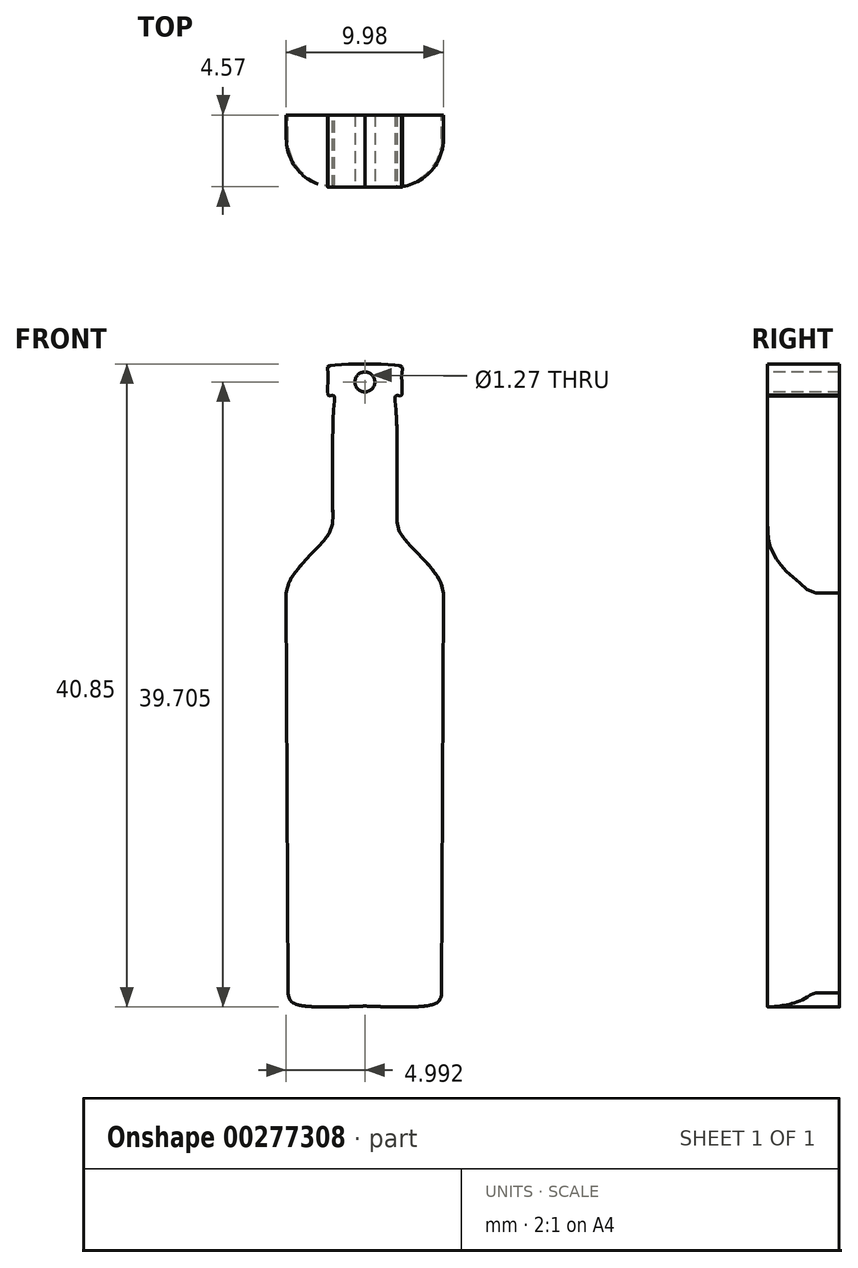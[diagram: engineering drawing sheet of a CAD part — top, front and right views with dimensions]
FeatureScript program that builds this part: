
annotation { "Feature Type Name" : "Feature", "Feature Type Description" : "" }
export const myFeature = defineFeature(function(context is Context, id is Id, definition is map)
    precondition{}
    {
        {
            var Q0;
            Q0=qCreatedBy(makeId("Front.planeOp"),FACE);
            var sketch = newSketch(context, id + "F0", { "sketchPlane" : qUnion([Q0])});
            skLineSegment(sketch, "E0", {"start": v(26.9, -30.26) * mm, "end": v(26.8, -4.86) * mm});
            skFitSpline(sketch, "E1", {"points": [v(26.8, -4.86) * mm, v(27.1, -3.94) * mm, v(28.53, -2.22) * mm, v(29.63, -0.84) * mm, v(29.74, 0.33) * mm, v(29.74, 2.9) * mm, v(29.8, 6.72) * mm, v(29.82, 7.68) * mm, v(29.66, 7.7) * mm, v(29.45, 7.71) * mm, v(29.44, 9.1) * mm, v(29.5, 9.55) * mm, v(31.72, 9.7) * mm, v(31.78, 9.7) * mm], "startDerivative": vector(2.33, 12.28) * mm, "endDerivative": vector(1.3, 0.77) * mm});
            skPoint(sketch, "E2", {"position": v(31.78, -31.09) * mm});
            skFitSpline(sketch, "E3", {"points": [v(26.9, -30.26) * mm, v(27.15, -30.83) * mm, v(28.84, -31.14) * mm, v(31.78, -31.09) * mm], "startDerivative": vector(0.53, -3.07) * mm, "endDerivative": vector(6.67, 0.25) * mm});
            skLineSegment(sketch, "E4", {"start": v(31.78, -31.09) * mm, "end": v(31.78, 9.7) * mm, "construction": true});
            skFitSpline(sketch, "E5.MirrorCS", {"points": [v(36.77, -4.86) * mm, v(36.47, -3.94) * mm, v(35.04, -2.22) * mm, v(33.94, -0.84) * mm, v(33.82, 0.33) * mm, v(33.82, 2.9) * mm, v(33.76, 6.72) * mm, v(33.74, 7.68) * mm, v(33.9, 7.7) * mm, v(34.11, 7.71) * mm, v(34.12, 9.1) * mm, v(34.06, 9.55) * mm, v(31.84, 9.7) * mm, v(31.78, 9.7) * mm], "startDerivative": vector(-2.33, 12.28) * mm, "endDerivative": vector(-1.3, 0.77) * mm});
            skLineSegment(sketch, "E6.MirrorCS", {"start": v(36.66, -30.26) * mm, "end": v(36.77, -4.86) * mm});
            skFitSpline(sketch, "E7.MirrorCS", {"points": [v(36.66, -30.26) * mm, v(36.41, -30.83) * mm, v(34.72, -31.14) * mm, v(31.78, -31.09) * mm], "startDerivative": vector(-0.53, -3.07) * mm, "endDerivative": vector(-6.67, 0.25) * mm});
            skSolve(sketch);
        }
        {
            var Q0;
            Q0=makeQuery(id+"F0.imprint","IMPRINT",FACE,{"disambiguationData":[TD([[makeQuery(id+"F0.imprint","IMPRINT",EDGE,{"derivedFrom":sQuery(id+"F0.wireOp",EDGE,"E0")}),-1.0]])]});
            extrude(context, id + "F1", {"entities" : qUnion([Q0]), "depth" : 4.57 * mm});
        }
        {
            var Q0;
            Q0=makeQuery(id+"F1.opExtrude","CAP_FACE",FACE,{"disambiguationData":[OSD([sQuery(id+"F0.wireOp",EDGE,"E0"),sQuery(id+"F0.wireOp",EDGE,"E1"),sQuery(id+"F0.wireOp",EDGE,"E3"),sQuery(id+"F0.wireOp",EDGE,"E5.MirrorCS"),sQuery(id+"F0.wireOp",EDGE,"E6.MirrorCS"),sQuery(id+"F0.wireOp",EDGE,"E7.MirrorCS")])],"isStart":false});
            var sketch = newSketch(context, id + "F2", { "sketchPlane" : qUnion([Q0])});
            skCircle(sketch, "E8", {"center": v(31.78, 8.55) * mm, "radius": 0.64 * mm});
            skSolve(sketch);
        }
        {
            var Q0;
            Q0=makeQuery(id+"F2.imprint","IMPRINT",FACE,{"disambiguationData":[TD([[makeQuery(id+"F2.imprint","IMPRINT",EDGE,{"derivedFrom":sQuery(id+"F2.wireOp",EDGE,"E8")}),1.0]])]});
            extrude(context, id + "F3", {"entities" : qUnion([Q0]), "operationType" : NewBodyOperationType.REMOVE, "oppositeDirection" : true, "depth" : 41.96 * mm});
        }
        {
            var Q0;
            Q0=makeQuery(id+"F1.opExtrude","CAP_EDGE",EDGE,{"disambiguationData":[OSD([sQuery(id+"F0.wireOp",EDGE,"E6.MirrorCS")])],"isStart":false});
            var Q1;
            Q1=makeQuery(id+"F1.opExtrude","CAP_EDGE",EDGE,{"disambiguationData":[OSD([sQuery(id+"F0.wireOp",EDGE,"E0")])],"isStart":false});
            fillet(context, id + "F4", {"entities" : qUnion([Q0, Q1]), "radius" : 3.07 * mm, "tangentPropagation" : true, "allowEdgeOverflow" : false});
        }
    });
